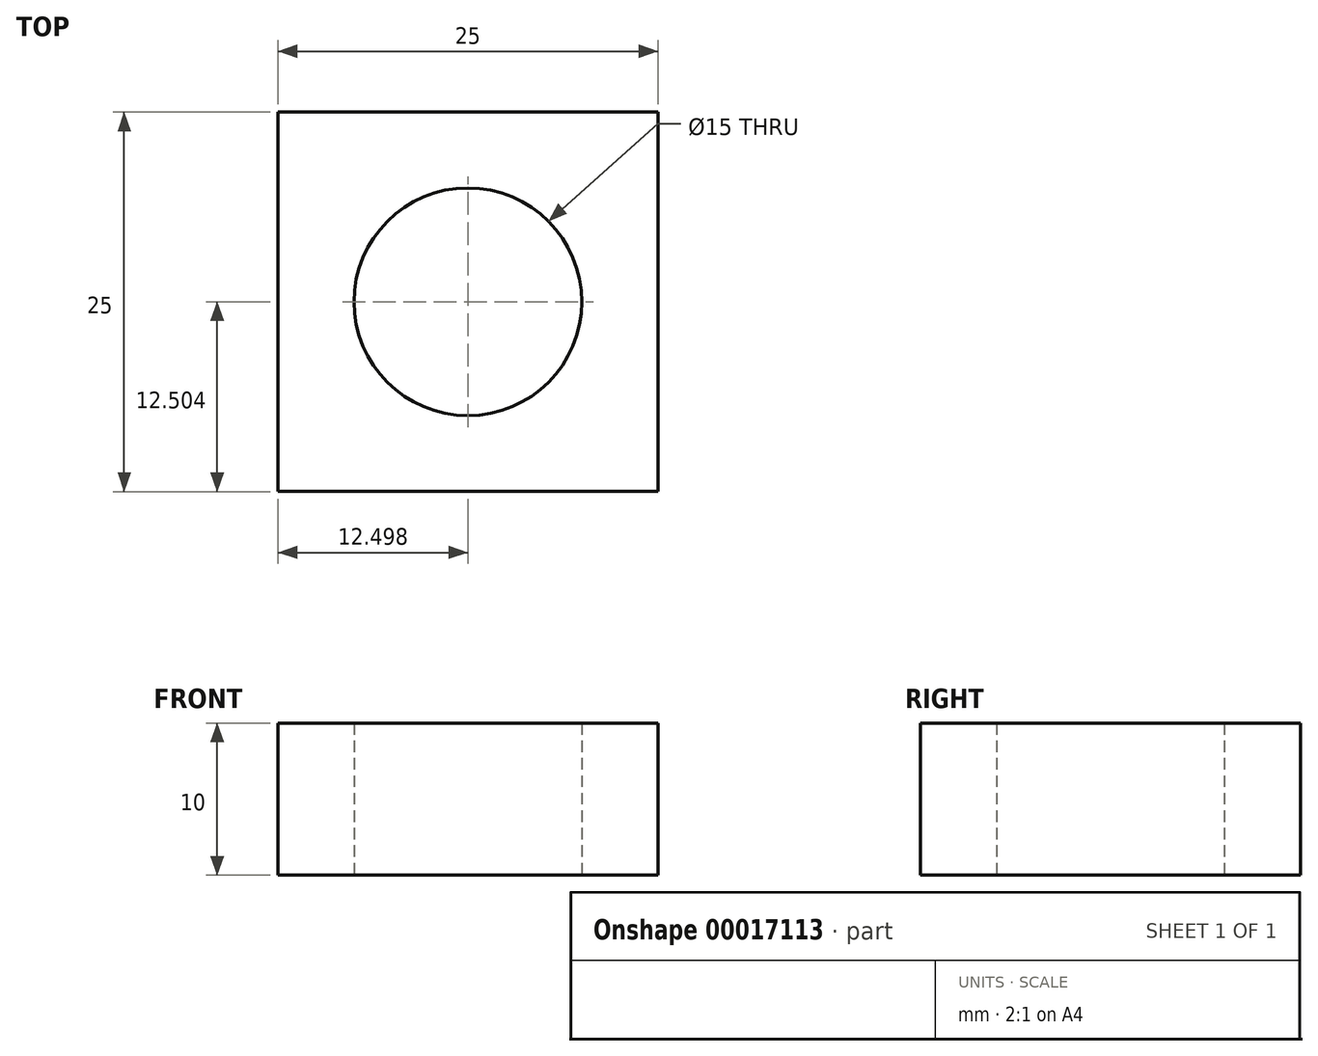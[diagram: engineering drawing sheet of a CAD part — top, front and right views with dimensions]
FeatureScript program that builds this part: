
annotation { "Feature Type Name" : "Feature", "Feature Type Description" : "" }
export const myFeature = defineFeature(function(context is Context, id is Id, definition is map)
    precondition{}
    {
        {
            var Q0;
            Q0=qCreatedBy(makeId("Top.planeOp"),FACE);
            var sketch = newSketch(context, id + "F0", { "sketchPlane" : qUnion([Q0])});
            skLineSegment(sketch, "E0.bottom", {"start": v(-50.64, 40.3) * mm, "end": v(-25.64, 40.3) * mm});
            skLineSegment(sketch, "E0.top", {"start": v(-50.64, 15.3) * mm, "end": v(-25.64, 15.3) * mm});
            skLineSegment(sketch, "E0.left", {"start": v(-50.64, 40.3) * mm, "end": v(-50.64, 15.3) * mm});
            skLineSegment(sketch, "E0.right", {"start": v(-25.64, 40.3) * mm, "end": v(-25.64, 15.3) * mm});
            skCircle(sketch, "E1", {"center": v(-38.14, 27.8) * mm, "radius": 7.5 * mm});
            skSolve(sketch);
        }
        {
            var Q0;
            Q0 = qSketchRegion(id + "F0", true);
            extrude(context, id + "F1", {"entities" : qUnion([Q0]), "depth" : 10 * mm});
        }
    });
